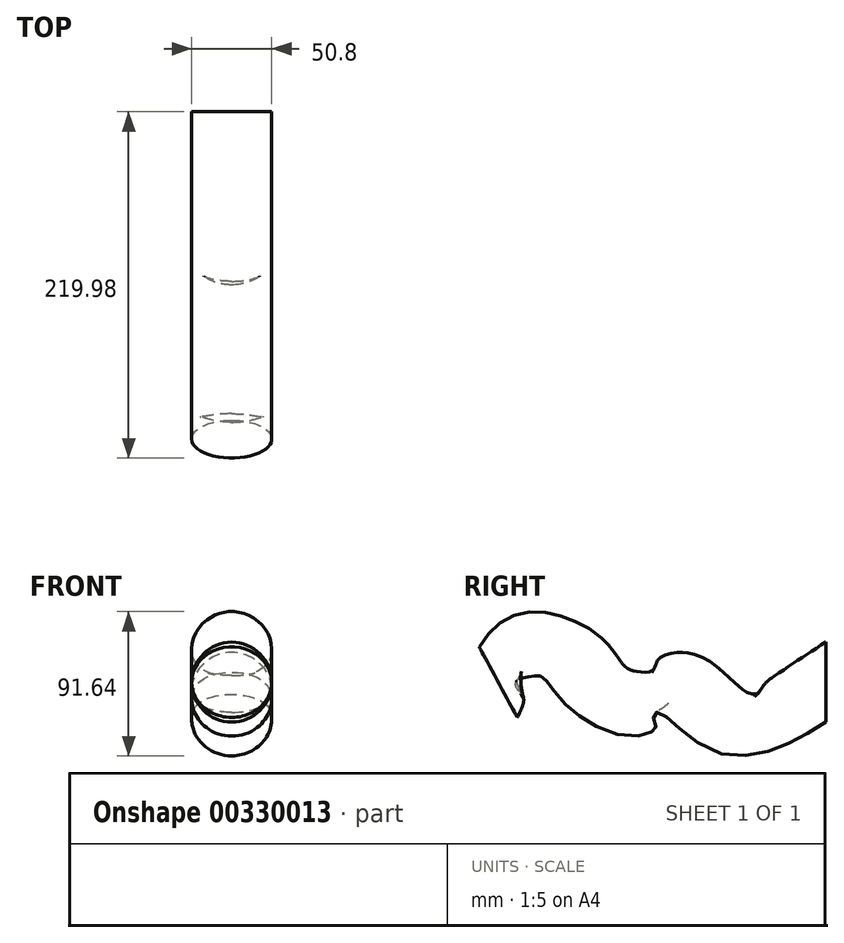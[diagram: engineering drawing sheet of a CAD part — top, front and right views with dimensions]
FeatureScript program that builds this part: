
annotation { "Feature Type Name" : "Feature", "Feature Type Description" : "" }
export const myFeature = defineFeature(function(context is Context, id is Id, definition is map)
    precondition{}
    {
        {
            var Q0;
            Q0=qCreatedBy(makeId("Front.planeOp"),FACE);
            var sketch = newSketch(context, id + "F0", { "sketchPlane" : qUnion([Q0])});
            skCircle(sketch, "E0", {"center": v(0, 0) * mm, "radius": 25.4 * mm});
            skSolve(sketch);
        }
        {
            var Q0;
            Q0=qCreatedBy(makeId("Right.planeOp"),FACE);
            var sketch = newSketch(context, id + "F1", { "sketchPlane" : qUnion([Q0])});
            skFitSpline(sketch, "E1", {"points": [v(0, 0) * mm, v(-59.52, -23.12) * mm, v(-92.06, -4.82) * mm, v(-119.17, -10.92) * mm, v(-146.97, 0) * mm, v(-161.88, 14.16) * mm, v(-189.67, 20.26) * mm, v(-207.98, 0) * mm], "startDerivative": vector(-321.84, -203.45) * mm, "endDerivative": vector(-114.5, -202.36) * mm});
            skSolve(sketch);
        }
        {
            var Q0;
            Q0=makeQuery(id+"F0.imprint","IMPRINT",FACE,{"disambiguationData":[TD([[makeQuery(id+"F0.imprint","IMPRINT",EDGE,{"derivedFrom":sQuery(id+"F0.wireOp",EDGE,"E0")}),1.0]])]});
            var Q1;
            Q1=sQuery(id+"F1.wireOp",EDGE,"E1");
            sweep(context, id + "F2", {"profiles" : qUnion([Q0]), "path" : qUnion([Q1])});
        }
    });
